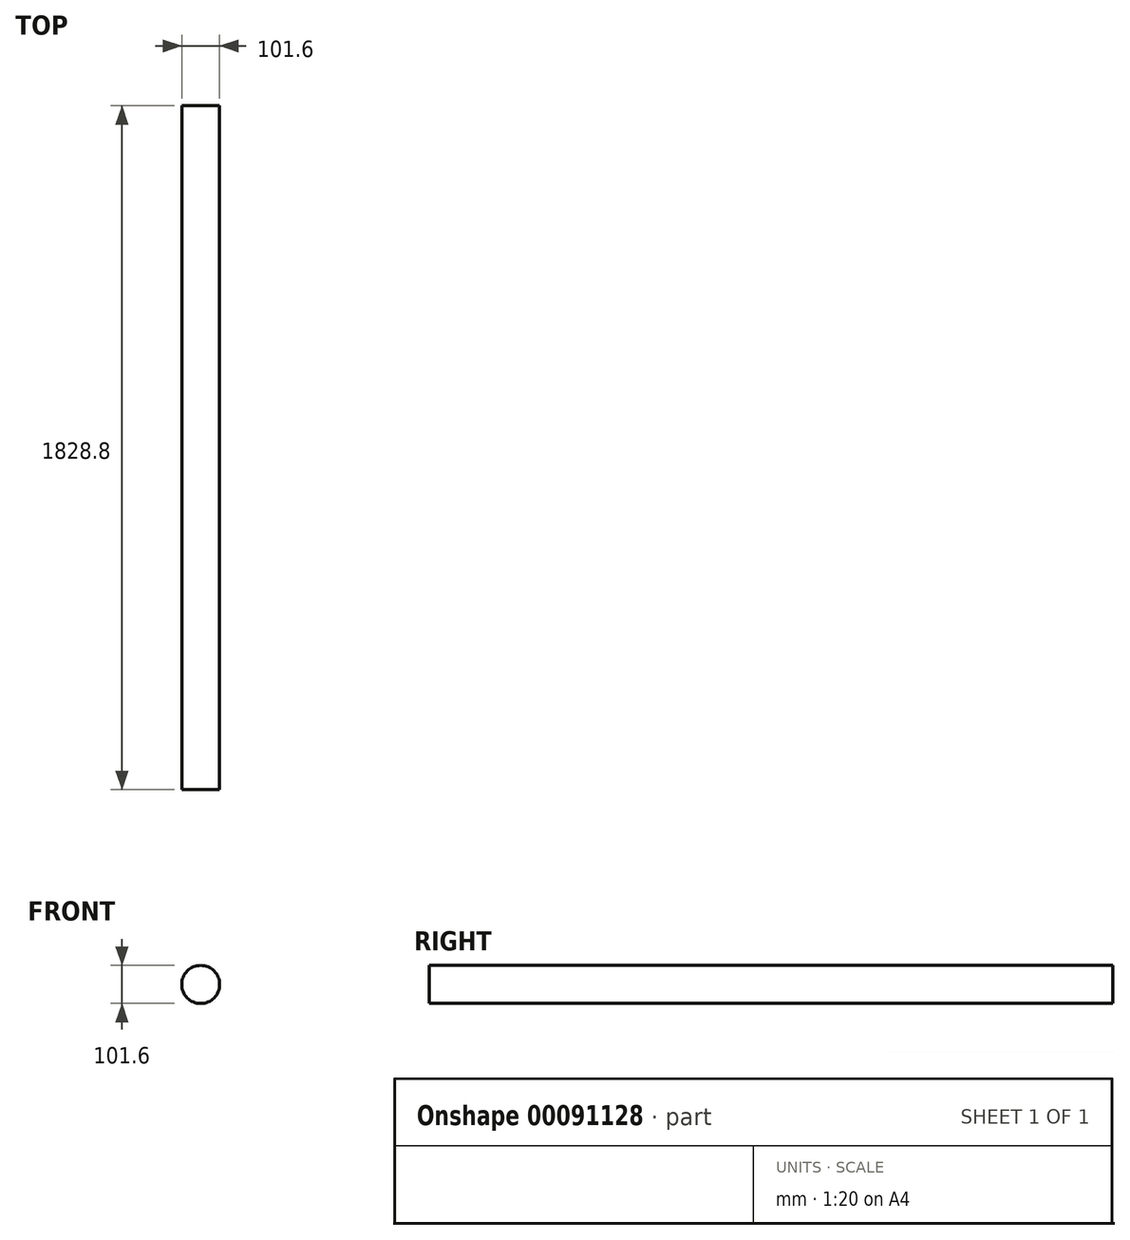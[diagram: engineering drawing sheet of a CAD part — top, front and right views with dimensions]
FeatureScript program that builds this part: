
annotation { "Feature Type Name" : "Feature", "Feature Type Description" : "" }
export const myFeature = defineFeature(function(context is Context, id is Id, definition is map)
    precondition{}
    {
        {
            var Q0;
            Q0=qCreatedBy(makeId("Front.planeOp"),FACE);
            var sketch = newSketch(context, id + "F0", { "sketchPlane" : qUnion([Q0])});
            skCircle(sketch, "E0", {"center": v(0, 0) * mm, "radius": 50.8 * mm});
            skSolve(sketch);
        }
        {
            var Q0;
            Q0 = qSketchRegion(id + "F0", true);
            extrude(context, id + "F1", {"entities" : qUnion([Q0]), "depth" : 1828.8 * mm});
        }
    });
